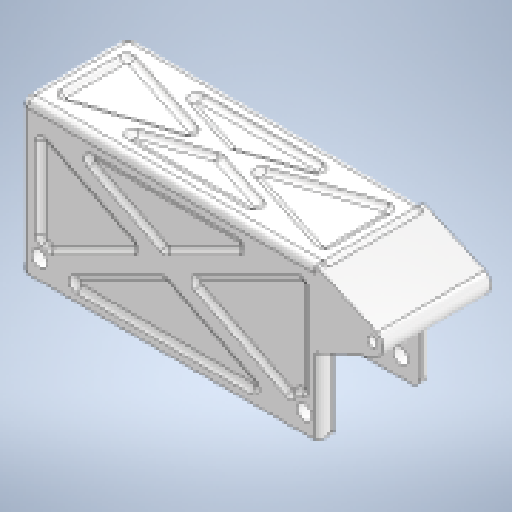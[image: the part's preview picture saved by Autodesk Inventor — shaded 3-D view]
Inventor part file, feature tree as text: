
AUTODESK INVENTOR PART (.ipt)
format: ipt  version: 2025.1 (Build 291241000, 241)  size: 674,816 bytes
history: native  units: mm
features: extrude x11, sketch x11, fillet x7, projected_geometry x7, other x1
ambient origin geometry x8: Origin, YZ Plane, XZ Plane, XY Plane, X Axis, Y Axis, Z Axis, Center Point
bodies: Body1 (feature_tree)
feature tree (37):
  other  "ソリッド1"
  extrude  "押し出し1"  Depth=80.0mm
  extrude  "押し出し2"  Depth=40.0mm
  extrude  "押し出し3"  Depth=3.0mm TaperAngle=0.0deg
  extrude  "押し出し4"  Depth=3.0mm
  extrude  "押し出し5"  Depth=22.5mm TaperAngle=0.0deg
  extrude  "押し出し6"  Depth=25.0mm
  fillet  "フィレット2"  Radius=20.0mm
  extrude  "押し出し7"  Depth=3.0mm TaperAngle=0.0deg
  extrude  "押し出し8"  Depth=15.0mm TaperAngle=0.0deg
  fillet  "フィレット3"  Radius=10.0mm
  extrude  "押し出し9"  Depth=4.0mm
  extrude  "押し出し10"  TaperAngle=0.0deg  [1 undecoded]
  fillet  "フィレット4"  Radius=2.0mm
  fillet  "フィレット5"  Radius=2.6mm
  fillet  "フィレット6"  Radius=6.0mm
  extrude  "押し出し11"  Depth=15.0mm
  fillet  "フィレット7"  Radius=10.0mm
  fillet  "フィレット8"  Radius=24.5mm
  sketch  "スケッチ1"
  sketch  "スケッチ2"
  projected_geometry  "投影ループ1"
  sketch  "スケッチ3"
  projected_geometry  "投影ループ2"
  sketch  "スケッチ4"
  projected_geometry  "投影ループ3"
  projected_geometry  "投影ループ4"
  sketch  "スケッチ5"
  sketch  "スケッチ6"
  sketch  "スケッチ7"
  sketch  "スケッチ8"
  projected_geometry  "投影ループ5"
  sketch  "スケッチ9"
  projected_geometry  "投影ループ6"
  sketch  "スケッチ10"
  projected_geometry  "投影ループ7"
  sketch  "スケッチ11"
note: 1 required parameter value undecoded (feature->parameter linkage not recoverable at this tier; creation-order binding heuristic only, values carry confidence <= 0.55)
